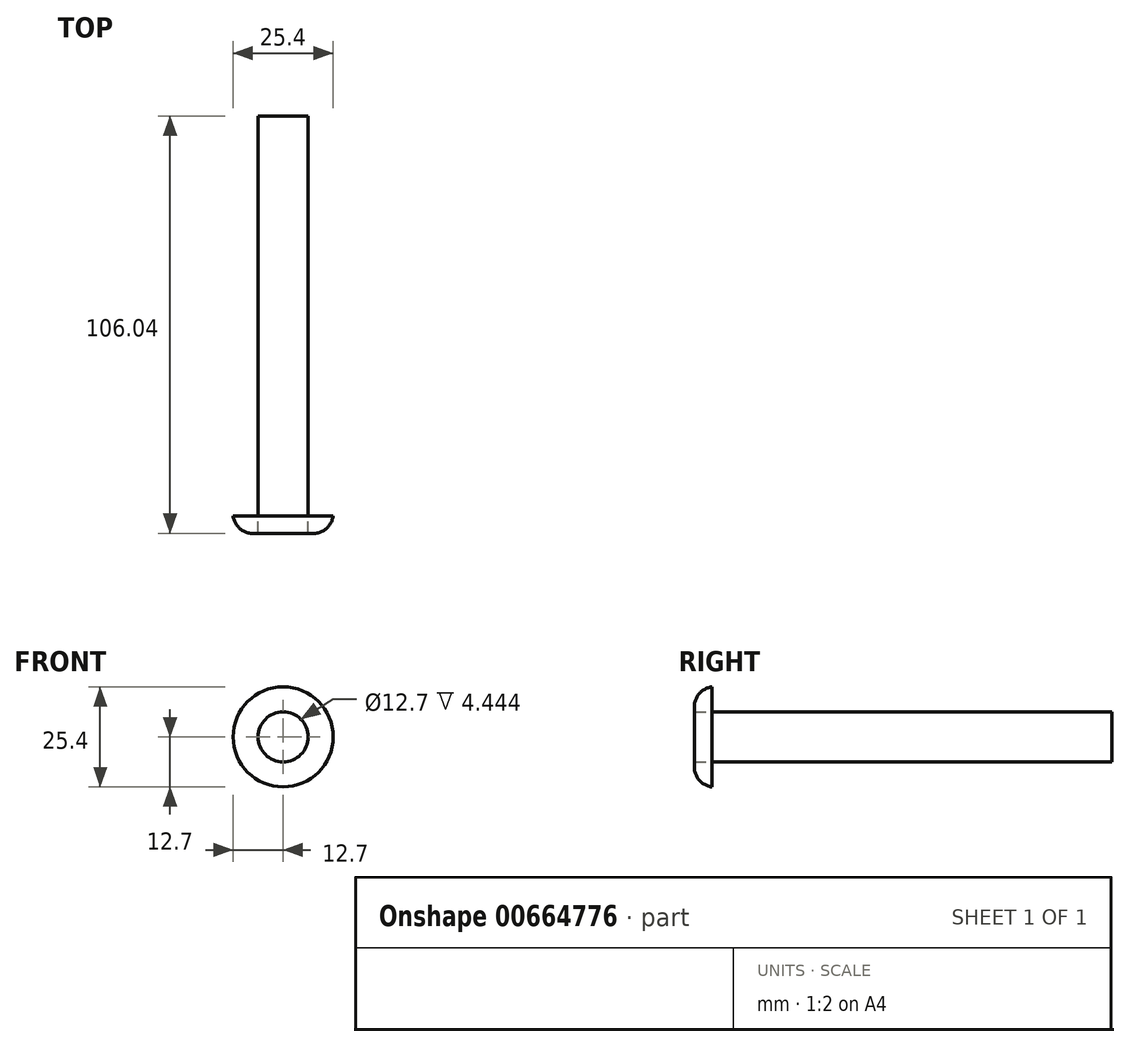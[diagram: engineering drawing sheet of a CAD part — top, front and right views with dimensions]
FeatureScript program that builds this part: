
annotation { "Feature Type Name" : "Feature", "Feature Type Description" : "" }
export const myFeature = defineFeature(function(context is Context, id is Id, definition is map)
    precondition{}
    {
        {
            var Q0;
            Q0=qCreatedBy(makeId("Front.planeOp"),FACE);
            var sketch = newSketch(context, id + "F0", { "sketchPlane" : qUnion([Q0])});
            skCircle(sketch, "E0", {"center": v(0, 0) * mm, "radius": 6.35 * mm});
            skCircle(sketch, "E1", {"center": v(0, 0) * mm, "radius": 12.7 * mm});
            skSolve(sketch);
        }
        {
            var Q0;
            Q0=makeQuery(id+"F0.imprint","IMPRINT",FACE,{"disambiguationData":[TD([[makeQuery(id+"F0.imprint","IMPRINT",EDGE,{"derivedFrom":sQuery(id+"F0.wireOp",EDGE,"E0")}),-1.0]])]});
            extrude(context, id + "F1", {"entities" : qUnion([Q0]), "depth" : 4.44 * mm, "offsetDistance" : 25.4 * mm});
        }
        {
            var Q0;
            Q0=makeQuery(id+"F1.opExtrude","CAP_EDGE",EDGE,{"disambiguationData":[OSD([sQuery(id+"F0.wireOp",EDGE,"E1")])],"isStart":false});
            fillet(context, id + "F2", {"entities" : qUnion([Q0]), "radius" : 5.08 * mm, "tangentPropagation" : true, "allowEdgeOverflow" : false});
        }
        {
            var Q0;
            Q0=qCreatedBy(makeId("Front.planeOp"),FACE);
            var sketch = newSketch(context, id + "F3", { "sketchPlane" : qUnion([Q0])});
            skCircle(sketch, "E2", {"center": v(0, 0) * mm, "radius": 6.35 * mm});
            skSolve(sketch);
        }
        {
            var Q0;
            Q0 = qSketchRegion(id + "F3", true);
            extrude(context, id + "F4", {"entities" : qUnion([Q0]), "oppositeDirection" : true, "depth" : 101.6 * mm, "offsetDistance" : 25.4 * mm});
        }
    });
